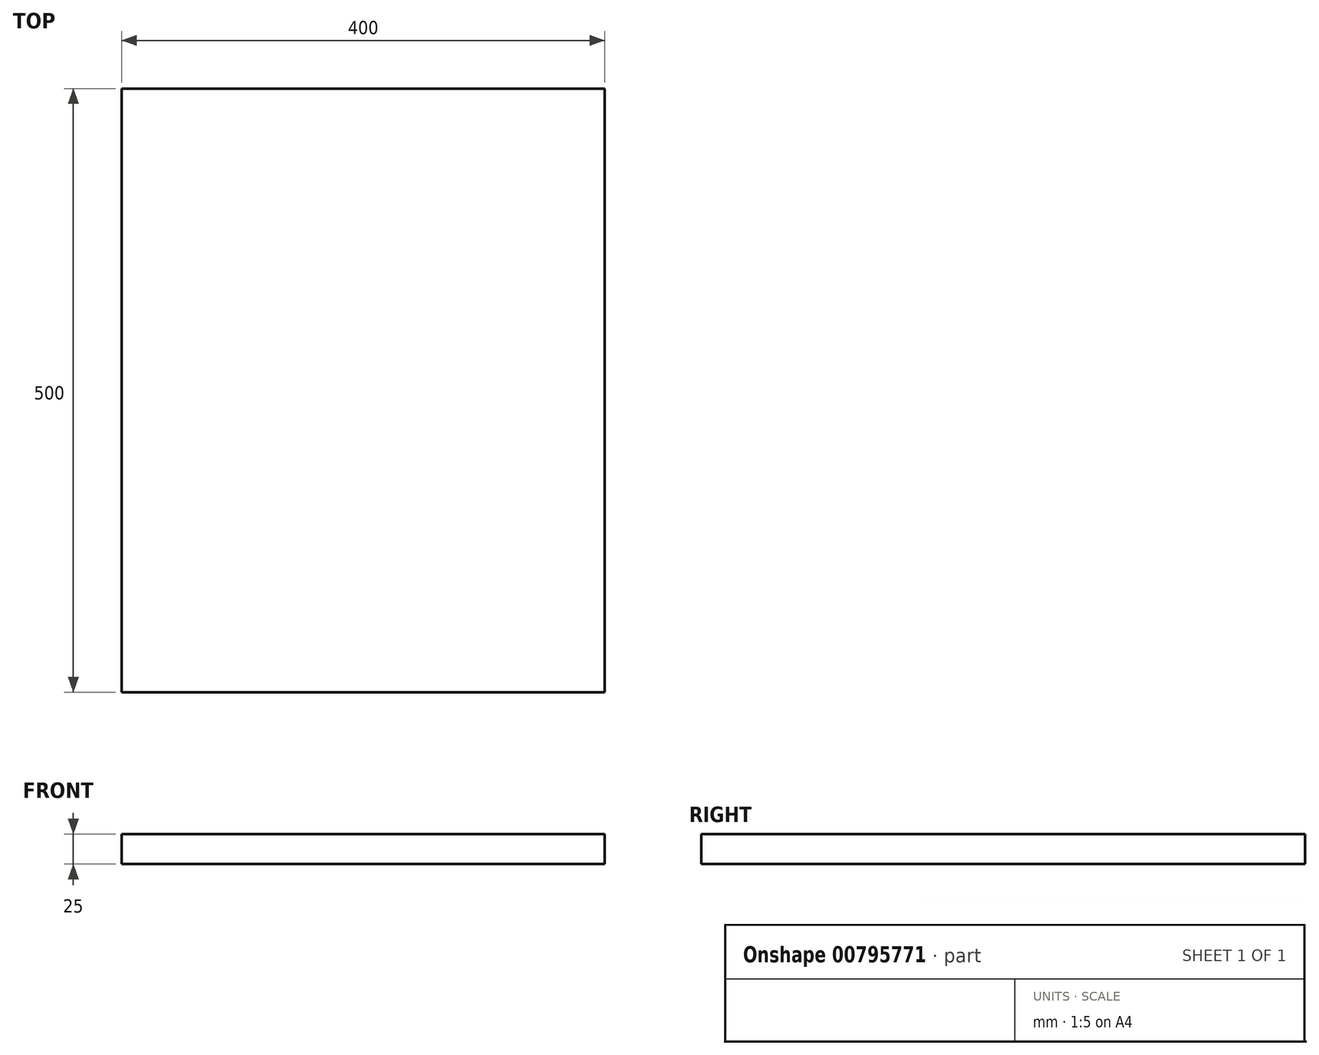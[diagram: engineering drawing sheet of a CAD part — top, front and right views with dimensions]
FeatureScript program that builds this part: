
annotation { "Feature Type Name" : "Feature", "Feature Type Description" : "" }
export const myFeature = defineFeature(function(context is Context, id is Id, definition is map)
    precondition{}
    {
        {
            var Q0;
            Q0=qCreatedBy(makeId("Top.planeOp"),FACE);
            var sketch = newSketch(context, id + "F0", { "sketchPlane" : qUnion([Q0])});
            skLineSegment(sketch, "E0.bottom", {"start": v(-202.69, 303.28) * mm, "end": v(197.31, 303.28) * mm});
            skLineSegment(sketch, "E0.top", {"start": v(-202.69, -196.72) * mm, "end": v(197.31, -196.72) * mm});
            skLineSegment(sketch, "E0.left", {"start": v(-202.69, 303.28) * mm, "end": v(-202.69, -196.72) * mm});
            skLineSegment(sketch, "E0.right", {"start": v(197.31, 303.28) * mm, "end": v(197.31, -196.72) * mm});
            skSolve(sketch);
        }
        {
            var Q0;
            Q0=makeQuery(id+"F0.imprint","IMPRINT",FACE,{"disambiguationData":[TD([[makeQuery(id+"F0.imprint","IMPRINT",EDGE,{"derivedFrom":sQuery(id+"F0.wireOp",EDGE,"E0.bottom")}),-1.0]])]});
            extrude(context, id + "F1", {"entities" : qUnion([Q0]), "depth" : 25 * mm, "offsetDistance" : 25 * mm});
        }
    });
